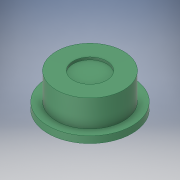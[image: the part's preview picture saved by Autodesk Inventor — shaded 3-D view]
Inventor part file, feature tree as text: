
AUTODESK INVENTOR PART (.ipt)
format: ipt  version: 2018 (Build 220112000, 112)  size: 115,712 bytes
history: native  units: in
note: dims shown in document units (in); Inventor stores cm internally (conversion verified against a paired STEP export)
features: extrude x3, sketch x3
ambient origin geometry x8: Origin, YZ Plane, XZ Plane, XY Plane, X Axis, Y Axis, Z Axis, Center Point
bodies: Solid1 (feature_tree)
feature tree (6):
  extrude  "Extrusion1"  Depth=1.2598in TaperAngle=0.0deg
  extrude  "Extrusion2"  Depth=0.315in TaperAngle=0.0deg
  extrude  "Extrusion3"  Depth=0.1181in TaperAngle=0.0deg
  sketch  "Sketch1"  dims[d0=3.1496in d1=1.2598in d2=0.0in]
  sketch  "Sketch2"  dims[d3=3.937in d4=0.315in d5=0.0in]
  sketch  "Sketch3"  dims[d6=1.5748in d7=0.1181in d8=0.0in]
